# Revit family: FU_Chair_Sandler_Woodlook_2-5C
name_source: partatom
category: Furniture
units: mm (PartAtom-declared; Revit-internal decimal feet)

## family parameters
Always vertical = Yes
Cut with Voids When Loaded = No
OmniClass Number = 23.40.20.00
OmniClass Title = General Furniture and Specialties
Room Calculation Point = No
Shared = No
Work Plane-Based = No

## types (1)
- FU_Chair_Sandler_Woodlook_2-5C
    Arm Height = 680 mm  [stored 2.23097 ft]
    Arm width = 595 mm  [stored 1.9521 ft]
    Default Elevation = 0 mm  [stored 0 ft]
    Depth = 512 mm  [stored 1.67979 ft]
    Description = Woodlook armchair with frame manufactured entirely from aluminum but with realistic appearance of wood. With casters in nylon (suitable for carpet floors) or polyurethane (suitable for wood or tile floors). Highly durable and scratch resistant.
    Manufacturer = Sandler
    Model = Woodlook 2.5C
    URL = https://www.sandlerseating.com
    Upholstery = Fabric - Gravity - Frozen CPC27
    Woodlook = Woodlook - 20A Natural Beech
    depth = 515 mm  [stored 1.68963 ft]

note: [stored X ft] marks values corroborated as IEEE doubles in the binary element streams (Revit-internal decimal feet)

## geometry (parser evidence)
native form markers: Sweep x3
no freeform markers — native parametric forms only
